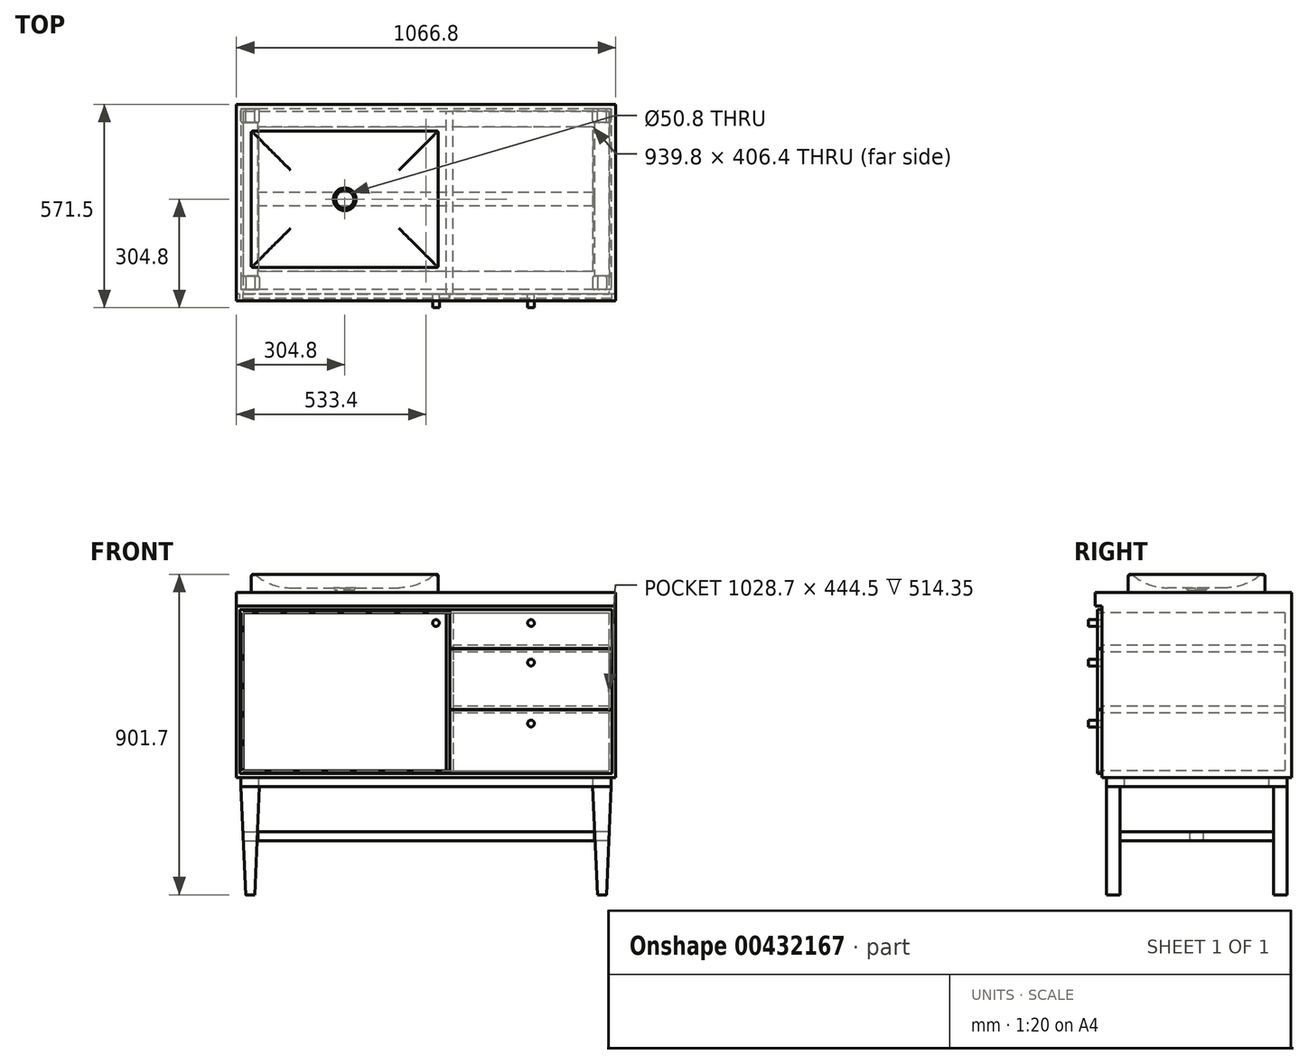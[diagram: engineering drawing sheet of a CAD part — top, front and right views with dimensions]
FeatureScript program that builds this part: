
annotation { "Feature Type Name" : "Feature", "Feature Type Description" : "" }
export const myFeature = defineFeature(function(context is Context, id is Id, definition is map)
    precondition{}
    {
        {
            var Q0;
            Q0=qCreatedBy(makeId("Front.planeOp"),FACE);
            var sketch = newSketch(context, id + "F0", { "sketchPlane" : qUnion([Q0])});
            skLineSegment(sketch, "E0.bottom", {"start": v(533.4, -241.3) * mm, "end": v(-533.4, -241.3) * mm});
            skLineSegment(sketch, "E0.top", {"start": v(533.4, 241.3) * mm, "end": v(-533.4, 241.3) * mm});
            skLineSegment(sketch, "E0.left", {"start": v(533.4, -241.3) * mm, "end": v(533.4, 241.3) * mm});
            skLineSegment(sketch, "E0.right", {"start": v(-533.4, -241.3) * mm, "end": v(-533.4, 241.3) * mm});
            skPoint(sketch, "E0.middle", {"position": v(0, 0) * mm});
            skSolve(sketch);
        }
        {
            var Q0;
            Q0=makeQuery(id+"F0.imprint","IMPRINT",FACE,{"disambiguationData":[TD([[makeQuery(id+"F0.imprint","IMPRINT",EDGE,{"derivedFrom":sQuery(id+"F0.wireOp",EDGE,"E0.bottom")}),-1.0]])]});
            extrude(context, id + "F1", {"entities" : qUnion([Q0]), "oppositeDirection" : true, "depth" : 533.4 * mm});
        }
        {
            var Q0;
            Q0=makeQuery(id+"F1.opExtrude","CAP_FACE",FACE,{"disambiguationData":[OSD([sQuery(id+"F0.wireOp",EDGE,"E0.bottom"),sQuery(id+"F0.wireOp",EDGE,"E0.top"),sQuery(id+"F0.wireOp",EDGE,"E0.left"),sQuery(id+"F0.wireOp",EDGE,"E0.right")])],"isStart":true});
            var sketch = newSketch(context, id + "F2", { "sketchPlane" : qUnion([Q0])});
            skLineSegment(sketch, "E1.bottom", {"start": v(-514.35, 222.25) * mm, "end": v(514.35, 222.25) * mm});
            skLineSegment(sketch, "E1.top", {"start": v(-514.35, -222.25) * mm, "end": v(514.35, -222.25) * mm});
            skLineSegment(sketch, "E1.left", {"start": v(-514.35, 222.25) * mm, "end": v(-514.35, -222.25) * mm});
            skLineSegment(sketch, "E1.right", {"start": v(514.35, 222.25) * mm, "end": v(514.35, -222.25) * mm});
            skPoint(sketch, "E1.middle", {"position": v(0, 0) * mm});
            skSolve(sketch);
        }
        {
            var Q0;
            Q0=makeQuery(id+"F2.imprint","IMPRINT",FACE,{"disambiguationData":[TD([[makeQuery(id+"F2.imprint","IMPRINT",EDGE,{"derivedFrom":sQuery(id+"F2.wireOp",EDGE,"E1.bottom")}),-1.0]])]});
            extrude(context, id + "F3", {"entities" : qUnion([Q0]), "operationType" : NewBodyOperationType.REMOVE, "oppositeDirection" : true, "depth" : 514.35 * mm});
        }
        {
            var Q0;
            Q0=makeQuery(id+"F1.opExtrude","SWEPT_FACE",FACE,{"disambiguationData":[OSD([sQuery(id+"F0.wireOp",EDGE,"E0.bottom")])]});
            var sketch = newSketch(context, id + "F4", { "sketchPlane" : qUnion([Q0])});
            skLineSegment(sketch, "E2.bottom", {"start": v(520.7, -520.7) * mm, "end": v(-520.7, -520.7) * mm});
            skLineSegment(sketch, "E2.top", {"start": v(520.7, -12.7) * mm, "end": v(-520.7, -12.7) * mm});
            skLineSegment(sketch, "E2.left", {"start": v(520.7, -520.7) * mm, "end": v(520.7, -12.7) * mm});
            skLineSegment(sketch, "E2.right", {"start": v(-520.7, -520.7) * mm, "end": v(-520.7, -12.7) * mm});
            skPoint(sketch, "E2.middle", {"position": v(0, -266.7) * mm});
            skPoint(sketch, "E2.middle.positionSnap0", {"position": v(-533.4, -266.7) * mm});
            skPoint(sketch, "E2.centerSnap0", {"position": v(-533.4, -266.7) * mm});
            skLineSegment(sketch, "E3.bottom", {"start": v(469.9, -63.5) * mm, "end": v(-469.9, -63.5) * mm});
            skLineSegment(sketch, "E3.top", {"start": v(469.9, -469.9) * mm, "end": v(-469.9, -469.9) * mm});
            skLineSegment(sketch, "E3.left", {"start": v(469.9, -63.5) * mm, "end": v(469.9, -469.9) * mm});
            skLineSegment(sketch, "E3.right", {"start": v(-469.9, -63.5) * mm, "end": v(-469.9, -469.9) * mm});
            skSolve(sketch);
        }
        {
            var Q0;
            Q0=makeQuery(id+"F4.imprint","IMPRINT",FACE,{"disambiguationData":[TD([[makeQuery(id+"F4.imprint","IMPRINT",EDGE,{"derivedFrom":sQuery(id+"F4.wireOp",EDGE,"E2.bottom")}),-1.0]])]});
            extrude(context, id + "F5", {"entities" : qUnion([Q0]), "depth" : 25.4 * mm});
        }
        {
            var Q0;
            Q0=makeQuery(id+"F5.opExtrude","SWEPT_FACE",FACE,{"disambiguationData":[OSD([sQuery(id+"F4.wireOp",EDGE,"E2.top")])]});
            var sketch = newSketch(context, id + "F6", { "sketchPlane" : qUnion([Q0])});
            skLineSegment(sketch, "E4", {"start": v(-520.7, -266.7) * mm, "end": v(-507.4, -571.5) * mm});
            skLineSegment(sketch, "E5", {"start": v(0, 222.25) * mm, "end": v(0, -222.25) * mm, "construction": true});
            skLineSegment(sketch, "E6.MirrorCS", {"start": v(520.7, -266.7) * mm, "end": v(507.4, -571.5) * mm});
            skLineSegment(sketch, "E7", {"start": v(-507.4, -571.5) * mm, "end": v(-482, -571.5) * mm});
            skLineSegment(sketch, "E8", {"start": v(-482, -571.5) * mm, "end": v(-468.68, -266.7) * mm});
            skLineSegment(sketch, "E9.MirrorCS", {"start": v(482, -571.5) * mm, "end": v(468.68, -266.7) * mm});
            skLineSegment(sketch, "E10.MirrorCS", {"start": v(507.4, -571.5) * mm, "end": v(482, -571.5) * mm});
            skLineSegment(sketch, "E11", {"start": v(-520.7, -266.7) * mm, "end": v(-468.68, -266.7) * mm});
            skLineSegment(sketch, "E12", {"start": v(468.68, -266.7) * mm, "end": v(520.7, -266.7) * mm});
            skSolve(sketch);
        }
        {
            var Q0;
            Q0=makeQuery(id+"F6.imprint","IMPRINT",FACE,{"disambiguationData":[TD([[makeQuery(id+"F6.imprint","IMPRINT",EDGE,{"derivedFrom":sQuery(id+"F6.wireOp",EDGE,"E4")}),1.0]])]});
            var Q1;
            Q1=makeQuery(id+"F6.imprint","IMPRINT",FACE,{"disambiguationData":[TD([[makeQuery(id+"F6.imprint","IMPRINT",EDGE,{"derivedFrom":sQuery(id+"F6.wireOp",EDGE,"E6.MirrorCS")}),-1.0]])]});
            extrude(context, id + "F7", {"entities" : qUnion([Q0, Q1]), "oppositeDirection" : true, "depth" : 38.1 * mm});
        }
        {
            var Q0;
            Q0=makeQuery(id+"F1.opExtrude","CAP_FACE",FACE,{"disambiguationData":[OSD([sQuery(id+"F0.wireOp",EDGE,"E0.bottom"),sQuery(id+"F0.wireOp",EDGE,"E0.top"),sQuery(id+"F0.wireOp",EDGE,"E0.left"),sQuery(id+"F0.wireOp",EDGE,"E0.right")])],"isStart":true});
            cPlane(context, id + "F8", {"entities" : qUnion([Q0]), "cplaneType" : CPlaneType.OFFSET, "offset" : 266.7 * mm, "oppositeDirection" : true, "width" : 152.4 * mm, "height" : 152.4 * mm});
        }
        {
            var Q0;
            Q0=makeQuery(id+"F7.opExtrude","SWEPT_BODY",BODY,{"disambiguationData":[OSD([sQuery(id+"F6.wireOp",EDGE,"E4"),sQuery(id+"F6.wireOp",EDGE,"E7"),sQuery(id+"F6.wireOp",EDGE,"E8"),sQuery(id+"F6.wireOp",EDGE,"E11")])]});
            var Q1;
            Q1=makeQuery(id+"F7.opExtrude","SWEPT_BODY",BODY,{"disambiguationData":[OSD([sQuery(id+"F6.wireOp",EDGE,"E6.MirrorCS"),sQuery(id+"F6.wireOp",EDGE,"E9.MirrorCS"),sQuery(id+"F6.wireOp",EDGE,"E10.MirrorCS"),sQuery(id+"F6.wireOp",EDGE,"E12")])]});
            var Q2;
            Q2=qCreatedBy(id+"F8.planeOp",FACE);
            mirror(context, id + "F9", {"entities" : qUnion([Q0, Q1]), "mirrorPlane" : qUnion([Q2])});
        }
        {
            var Q0;
            Q0=makeQuery(id+"F7.opExtrude","SWEPT_FACE",FACE,{"disambiguationData":[OSD([sQuery(id+"F6.wireOp",EDGE,"E4")])]});
            var sketch = newSketch(context, id + "F10", { "sketchPlane" : qUnion([Q0])});
            skLineSegment(sketch, "E13.bottom", {"start": v(-50.8, -370.73) * mm, "end": v(-482.6, -370.73) * mm});
            skLineSegment(sketch, "E13.top", {"start": v(-50.8, -396.13) * mm, "end": v(-482.6, -396.13) * mm});
            skLineSegment(sketch, "E13.left", {"start": v(-50.8, -370.73) * mm, "end": v(-50.8, -396.13) * mm});
            skLineSegment(sketch, "E13.right", {"start": v(-482.6, -370.73) * mm, "end": v(-482.6, -396.13) * mm});
            skPoint(sketch, "E13.middle", {"position": v(-266.7, -383.43) * mm});
            skSolve(sketch);
        }
        {
            var Q0;
            Q0=makeQuery(id+"F9.opPattern","COPY",FACE,{"derivedFrom":makeQuery(id+"F7.opExtrude","CAP_FACE",FACE,{"disambiguationData":[OSD([sQuery(id+"F6.wireOp",EDGE,"E4"),sQuery(id+"F6.wireOp",EDGE,"E7"),sQuery(id+"F6.wireOp",EDGE,"E8"),sQuery(id+"F6.wireOp",EDGE,"E11")])],"isStart":false}),"instanceName":"1"});
            var sketch = newSketch(context, id + "F11", { "sketchPlane" : qUnion([Q0])});
            skLineSegment(sketch, "E14", {"start": v(-515.16, -393.58) * mm, "end": v(-474.22, -393.58) * mm});
            skSolve(sketch);
        }
        {
            var Q0;
            Q0=makeQuery(id+"F10.imprint","IMPRINT",FACE,{"disambiguationData":[TD([[makeQuery(id+"F10.imprint","IMPRINT",EDGE,{"derivedFrom":sQuery(id+"F10.wireOp",EDGE,"E13.bottom")}),1.0]])]});
            var Q1;
            Q1=sQuery(id+"F11.wireOp",EDGE,"E14");
            sweep(context, id + "F12", {"profiles" : qUnion([Q0]), "path" : qUnion([Q1])});
        }
        {
            var Q0;
            Q0=makeQuery(id+"F12.opSweep","SWEPT_BODY",BODY,{"disambiguationData":[OSD([sQuery(id+"F10.wireOp",EDGE,"E13.bottom"),sQuery(id+"F10.wireOp",EDGE,"E13.top"),sQuery(id+"F10.wireOp",EDGE,"E13.left"),sQuery(id+"F10.wireOp",EDGE,"E13.right"),sQuery(id+"F11.wireOp",EDGE,"E14")])]});
            var Q1;
            Q1=qCreatedBy(makeId("Right.planeOp"),FACE);
            mirror(context, id + "F13", {"entities" : qUnion([Q0]), "mirrorPlane" : qUnion([Q1])});
        }
        {
            var Q0;
            Q0=makeQuery(id+"F12.opSweep","SWEPT_FACE",FACE,{"disambiguationData":[OSD([sQuery(id+"F10.wireOp",EDGE,"E13.bottom"),sQuery(id+"F11.wireOp",EDGE,"E14")])]});
            var sketch = newSketch(context, id + "F14", { "sketchPlane" : qUnion([Q0])});
            skLineSegment(sketch, "E15.bottom", {"start": v(473.12, 285.75) * mm, "end": v(-473.12, 285.75) * mm});
            skLineSegment(sketch, "E15.top", {"start": v(473.12, 247.65) * mm, "end": v(-473.12, 247.65) * mm});
            skLineSegment(sketch, "E15.left", {"start": v(473.12, 285.75) * mm, "end": v(473.12, 247.65) * mm});
            skLineSegment(sketch, "E15.right", {"start": v(-473.12, 285.75) * mm, "end": v(-473.12, 247.65) * mm});
            skPoint(sketch, "E15.middle", {"position": v(0, 266.7) * mm});
            skPoint(sketch, "E15.middle.positionSnap0", {"position": v(-474.22, 266.7) * mm});
            skPoint(sketch, "E15.centerSnap0", {"position": v(-474.22, 266.7) * mm});
            skSolve(sketch);
        }
        {
            var Q0;
            Q0=makeQuery(id+"F14.imprint","IMPRINT",FACE,{"disambiguationData":[TD([[makeQuery(id+"F14.imprint","IMPRINT",EDGE,{"derivedFrom":sQuery(id+"F14.wireOp",EDGE,"E15.bottom")}),1.0]])]});
            var Q1;
            Q1=makeQuery(id+"F12.opSweep","SWEPT_FACE",FACE,{"disambiguationData":[OSD([sQuery(id+"F10.wireOp",EDGE,"E13.top"),sQuery(id+"F11.wireOp",EDGE,"E14")])]});
            extrude(context, id + "F15", {"entities" : qUnion([Q0]), "endBound" : BoundingType.UP_TO_SURFACE, "oppositeDirection" : true, "endBoundEntityFace" : qUnion([Q1]), "depth" : 25.4 * mm});
        }
        {
            var Q0;
            Q0=makeQuery(id+"F1.opExtrude","SWEPT_FACE",FACE,{"disambiguationData":[OSD([sQuery(id+"F0.wireOp",EDGE,"E0.top")])]});
            var sketch = newSketch(context, id + "F16", { "sketchPlane" : qUnion([Q0])});
            skLineSegment(sketch, "E16.bottom", {"start": v(-533.4, 533.4) * mm, "end": v(533.4, 533.4) * mm});
            skLineSegment(sketch, "E16.top", {"start": v(-533.4, 0) * mm, "end": v(533.4, 0) * mm});
            skLineSegment(sketch, "E16.left", {"start": v(-533.4, 533.4) * mm, "end": v(-533.4, 0) * mm});
            skLineSegment(sketch, "E16.right", {"start": v(533.4, 533.4) * mm, "end": v(533.4, 0) * mm});
            skPoint(sketch, "E16.middle", {"position": v(0, 266.7) * mm});
            skPoint(sketch, "E16.middle.positionSnap0", {"position": v(0, 533.4) * mm});
            skPoint(sketch, "E16.middle.positionSnap1", {"position": v(-533.4, 266.7) * mm});
            skPoint(sketch, "E16.centerSnap0", {"position": v(0, 533.4) * mm});
            skPoint(sketch, "E16.centerSnap1", {"position": v(-533.4, 266.7) * mm});
            skSolve(sketch);
        }
        {
            var Q0;
            Q0 = qSketchRegion(id + "F16", true);
            extrude(context, id + "F17", {"entities" : qUnion([Q0]), "depth" : 38.1 * mm});
        }
        {
            var Q0;
            Q0=makeQuery(id+"F17.opExtrude","CAP_FACE",FACE,{"disambiguationData":[OSD([sQuery(id+"F16.wireOp",EDGE,"E16.bottom"),sQuery(id+"F16.wireOp",EDGE,"E16.top"),sQuery(id+"F16.wireOp",EDGE,"E16.left"),sQuery(id+"F16.wireOp",EDGE,"E16.right")])],"isStart":false});
            var sketch = newSketch(context, id + "F18", { "sketchPlane" : qUnion([Q0])});
            skLineSegment(sketch, "E17.bottom", {"start": v(-491.33, 74.61) * mm, "end": v(34.13, 74.61) * mm});
            skLineSegment(sketch, "E17.top", {"start": v(-491.33, 458.79) * mm, "end": v(34.13, 458.79) * mm});
            skLineSegment(sketch, "E17.left", {"start": v(-491.33, 74.61) * mm, "end": v(-491.33, 458.79) * mm});
            skLineSegment(sketch, "E17.right", {"start": v(34.13, 74.61) * mm, "end": v(34.13, 458.79) * mm});
            skPoint(sketch, "E17.middle", {"position": v(-228.6, 266.7) * mm});
            skPoint(sketch, "E17.middle.positionSnap0", {"position": v(533.4, 266.7) * mm});
            skPoint(sketch, "E17.centerSnap0", {"position": v(533.4, 266.7) * mm});
            skSolve(sketch);
        }
        {
            var Q0;
            Q0=makeQuery(id+"F18.imprint","IMPRINT",FACE,{"disambiguationData":[TD([[makeQuery(id+"F18.imprint","IMPRINT",EDGE,{"derivedFrom":sQuery(id+"F18.wireOp",EDGE,"E17.bottom")}),1.0]])]});
            extrude(context, id + "F19", {"entities" : qUnion([Q0]), "depth" : 50.8 * mm});
        }
        {
            var Q0;
            Q0=makeQuery(id+"F19.opExtrude","SWEPT_EDGE",EDGE,{"disambiguationData":[OSD([sQuery(id+"F18.wireOp",EDGE,"E17.bottom"),sQuery(id+"F18.wireOp",EDGE,"E17.left")])]});
            var Q1;
            Q1=makeQuery(id+"F19.opExtrude","SWEPT_EDGE",EDGE,{"disambiguationData":[OSD([sQuery(id+"F18.wireOp",EDGE,"E17.bottom"),sQuery(id+"F18.wireOp",EDGE,"E17.right")])]});
            var Q2;
            Q2=makeQuery(id+"F19.opExtrude","SWEPT_EDGE",EDGE,{"disambiguationData":[OSD([sQuery(id+"F18.wireOp",EDGE,"E17.top"),sQuery(id+"F18.wireOp",EDGE,"E17.right")])]});
            var Q3;
            Q3=makeQuery(id+"F19.opExtrude","SWEPT_EDGE",EDGE,{"disambiguationData":[OSD([sQuery(id+"F18.wireOp",EDGE,"E17.top"),sQuery(id+"F18.wireOp",EDGE,"E17.left")])]});
            fillet(context, id + "F20", {"entities" : qUnion([Q0, Q1, Q2, Q3]), "radius" : (4 + (9 / 16)) * mm, "tangentPropagation" : true, "allowEdgeOverflow" : false});
        }
        {
            var Q0;
            Q0=makeQuery(id+"F19.opExtrude","CAP_FACE",FACE,{"disambiguationData":[OSD([sQuery(id+"F18.wireOp",EDGE,"E17.bottom"),sQuery(id+"F18.wireOp",EDGE,"E17.top"),sQuery(id+"F18.wireOp",EDGE,"E17.left"),sQuery(id+"F18.wireOp",EDGE,"E17.right")])],"isStart":false});
            shell(context, id + "F21", {"entities" : qUnion([Q0]), "thickness" : 12.7 * mm});
        }
        {
            var Q0;
            Q0=makeQuery(id+"F19.opExtrude","CAP_FACE",FACE,{"disambiguationData":[OSD([sQuery(id+"F18.wireOp",EDGE,"E17.bottom"),sQuery(id+"F18.wireOp",EDGE,"E17.top"),sQuery(id+"F18.wireOp",EDGE,"E17.left"),sQuery(id+"F18.wireOp",EDGE,"E17.right")])],"isStart":false});
            fillet(context, id + "F22", {"entities" : qUnion([Q0]), "radius" : 5.08 * mm, "tangentPropagation" : true, "allowEdgeOverflow" : false});
        }
        {
            var Q0;
            Q0=makeQuery(id+"F21.opShell","OFFSET_FACE",FACE,{"disambiguationData":[OSD([sQuery(id+"F18.wireOp",EDGE,"E17.bottom"),sQuery(id+"F18.wireOp",EDGE,"E17.top"),sQuery(id+"F18.wireOp",EDGE,"E17.left"),sQuery(id+"F18.wireOp",EDGE,"E17.right")])]});
            fillet(context, id + "F23", {"entities" : qUnion([Q0]), "radius" : 152.4 * mm, "tangentPropagation" : true, "allowEdgeOverflow" : false});
        }
        {
            var Q0;
            Q0=makeQuery(id+"F21.opShell","OFFSET_FACE",FACE,{"disambiguationData":[OSD([sQuery(id+"F18.wireOp",EDGE,"E17.bottom"),sQuery(id+"F18.wireOp",EDGE,"E17.top"),sQuery(id+"F18.wireOp",EDGE,"E17.left"),sQuery(id+"F18.wireOp",EDGE,"E17.right")])]});
            var sketch = newSketch(context, id + "F24", { "sketchPlane" : qUnion([Q0])});
            skPoint(sketch, "E18", {"position": v(-228.6, 266.7) * mm});
            skPoint(sketch, "E18.positionSnap0", {"position": v(-381, 266.7) * mm});
            skPoint(sketch, "E18.positionSnap1", {"position": v(-228.6, 348.46) * mm});
            skSolve(sketch);
        }
        {
            var Q0;
            Q0=sQuery(id+"F24.wireOp",VERTEX,"E18");
            var Q1;
            Q1=makeQuery(id+"F19.opExtrude","SWEPT_BODY",BODY,{"disambiguationData":[OSD([sQuery(id+"F18.wireOp",EDGE,"E17.bottom"),sQuery(id+"F18.wireOp",EDGE,"E17.top"),sQuery(id+"F18.wireOp",EDGE,"E17.left"),sQuery(id+"F18.wireOp",EDGE,"E17.right")])]});
            hole(context, id + "F25", {"style" : HoleStyle.C_SINK, "endStyle" : HoleEndStyle.BLIND, "holeDiameter" : 50.8 * mm, "cSinkDiameter" : 63.5 * mm, "cSinkAngle" : 82 * degree, "holeDepth" : 25.4 * mm, "isTappedThrough" : true, "tappedDepth" : 12.7 * mm, "tapClearance" : 3, "locations" : qUnion([Q0]), "scope" : qUnion([Q1])});
        }
        {
            var Q0;
            Q0=makeQuery(id+"F12.opSweep","CAP_EDGE",EDGE,{"disambiguationData":[OSD([sQuery(id+"F10.wireOp",EDGE,"E13.top"),sQuery(id+"F11.wireOp",VERTEX,"E14.end")])],"isStart":false});
            var Q1;
            Q1=makeQuery(id+"F12.opSweep","CAP_EDGE",EDGE,{"disambiguationData":[OSD([sQuery(id+"F10.wireOp",EDGE,"E13.bottom"),sQuery(id+"F11.wireOp",VERTEX,"E14.end")])],"isStart":false});
            var Q2;
            Q2=makeQuery(id+"F12.opSweep","CAP_EDGE",EDGE,{"disambiguationData":[OSD([sQuery(id+"F10.wireOp",EDGE,"E13.bottom"),sQuery(id+"F11.wireOp",VERTEX,"E14.start")])],"isStart":true});
            var Q3;
            Q3=makeQuery(id+"F12.opSweep","CAP_EDGE",EDGE,{"disambiguationData":[OSD([sQuery(id+"F10.wireOp",EDGE,"E13.top"),sQuery(id+"F11.wireOp",VERTEX,"E14.start")])],"isStart":true});
            var Q4;
            Q4=makeQuery(id+"F9.opPattern","COPY",EDGE,{"derivedFrom":makeQuery(id+"F7.opExtrude","CAP_EDGE",EDGE,{"disambiguationData":[OSD([sQuery(id+"F6.wireOp",EDGE,"E4")])],"isStart":false}),"instanceName":"1"});
            var Q5;
            Q5=makeQuery(id+"F9.opPattern","COPY",EDGE,{"derivedFrom":makeQuery(id+"F7.opExtrude","CAP_EDGE",EDGE,{"disambiguationData":[OSD([sQuery(id+"F6.wireOp",EDGE,"E8")])],"isStart":false}),"instanceName":"1"});
            var Q6;
            Q6=makeQuery(id+"F9.opPattern","COPY",EDGE,{"derivedFrom":makeQuery(id+"F7.opExtrude","CAP_EDGE",EDGE,{"disambiguationData":[OSD([sQuery(id+"F6.wireOp",EDGE,"E4")])],"isStart":true}),"instanceName":"1"});
            var Q7;
            Q7=makeQuery(id+"F15.opExtrude","CAP_EDGE",EDGE,{"disambiguationData":[OSD([sQuery(id+"F14.wireOp",EDGE,"E15.top")])],"isStart":true});
            var Q8;
            Q8=makeQuery(id+"F7.opExtrude","CAP_EDGE",EDGE,{"disambiguationData":[OSD([sQuery(id+"F6.wireOp",EDGE,"E4")])],"isStart":true});
            var Q9;
            Q9=makeQuery(id+"F7.opExtrude","CAP_EDGE",EDGE,{"disambiguationData":[OSD([sQuery(id+"F6.wireOp",EDGE,"E4")])],"isStart":false});
            var Q10;
            Q10=makeQuery(id+"F7.opExtrude","CAP_EDGE",EDGE,{"disambiguationData":[OSD([sQuery(id+"F6.wireOp",EDGE,"E8")])],"isStart":true});
            var Q11;
            Q11=makeQuery(id+"F7.opExtrude","CAP_EDGE",EDGE,{"disambiguationData":[OSD([sQuery(id+"F6.wireOp",EDGE,"E8")])],"isStart":false});
            var Q12;
            Q12=makeQuery(id+"F9.opPattern","COPY",EDGE,{"derivedFrom":makeQuery(id+"F7.opExtrude","CAP_EDGE",EDGE,{"disambiguationData":[OSD([sQuery(id+"F6.wireOp",EDGE,"E8")])],"isStart":true}),"instanceName":"1"});
            var Q13;
            Q13=makeQuery(id+"F15.opExtrude","CAP_EDGE",EDGE,{"disambiguationData":[OSD([sQuery(id+"F14.wireOp",EDGE,"E15.top")])],"isStart":false});
            var Q14;
            Q14=makeQuery(id+"F15.opExtrude","CAP_EDGE",EDGE,{"disambiguationData":[OSD([sQuery(id+"F14.wireOp",EDGE,"E15.bottom")])],"isStart":true});
            var Q15;
            Q15=makeQuery(id+"F15.opExtrude","CAP_EDGE",EDGE,{"disambiguationData":[OSD([sQuery(id+"F14.wireOp",EDGE,"E15.bottom")])],"isStart":false});
            var Q16;
            Q16=makeQuery(id+"F13.opPattern","COPY",EDGE,{"derivedFrom":makeQuery(id+"F12.opSweep","CAP_EDGE",EDGE,{"disambiguationData":[OSD([sQuery(id+"F10.wireOp",EDGE,"E13.top"),sQuery(id+"F11.wireOp",VERTEX,"E14.end")])],"isStart":false}),"instanceName":"1"});
            var Q17;
            Q17=makeQuery(id+"F13.opPattern","COPY",EDGE,{"derivedFrom":makeQuery(id+"F12.opSweep","CAP_EDGE",EDGE,{"disambiguationData":[OSD([sQuery(id+"F10.wireOp",EDGE,"E13.bottom"),sQuery(id+"F11.wireOp",VERTEX,"E14.end")])],"isStart":false}),"instanceName":"1"});
            var Q18;
            Q18=makeQuery(id+"F9.opPattern","COPY",EDGE,{"derivedFrom":makeQuery(id+"F7.opExtrude","CAP_EDGE",EDGE,{"disambiguationData":[OSD([sQuery(id+"F6.wireOp",EDGE,"E9.MirrorCS")])],"isStart":false}),"instanceName":"1"});
            var Q19;
            Q19=makeQuery(id+"F9.opPattern","COPY",EDGE,{"derivedFrom":makeQuery(id+"F7.opExtrude","CAP_EDGE",EDGE,{"disambiguationData":[OSD([sQuery(id+"F6.wireOp",EDGE,"E9.MirrorCS")])],"isStart":true}),"instanceName":"1"});
            var Q20;
            Q20=makeQuery(id+"F9.opPattern","COPY",EDGE,{"derivedFrom":makeQuery(id+"F7.opExtrude","CAP_EDGE",EDGE,{"disambiguationData":[OSD([sQuery(id+"F6.wireOp",EDGE,"E6.MirrorCS")])],"isStart":true}),"instanceName":"1"});
            var Q21;
            Q21=makeQuery(id+"F9.opPattern","COPY",EDGE,{"derivedFrom":makeQuery(id+"F7.opExtrude","CAP_EDGE",EDGE,{"disambiguationData":[OSD([sQuery(id+"F6.wireOp",EDGE,"E6.MirrorCS")])],"isStart":false}),"instanceName":"1"});
            var Q22;
            Q22=makeQuery(id+"F13.opPattern","COPY",EDGE,{"derivedFrom":makeQuery(id+"F12.opSweep","CAP_EDGE",EDGE,{"disambiguationData":[OSD([sQuery(id+"F10.wireOp",EDGE,"E13.bottom"),sQuery(id+"F11.wireOp",VERTEX,"E14.start")])],"isStart":true}),"instanceName":"1"});
            var Q23;
            Q23=makeQuery(id+"F13.opPattern","COPY",EDGE,{"derivedFrom":makeQuery(id+"F12.opSweep","CAP_EDGE",EDGE,{"disambiguationData":[OSD([sQuery(id+"F10.wireOp",EDGE,"E13.top"),sQuery(id+"F11.wireOp",VERTEX,"E14.start")])],"isStart":true}),"instanceName":"1"});
            var Q24;
            Q24=makeQuery(id+"F7.opExtrude","CAP_EDGE",EDGE,{"disambiguationData":[OSD([sQuery(id+"F6.wireOp",EDGE,"E6.MirrorCS")])],"isStart":true});
            var Q25;
            Q25=makeQuery(id+"F7.opExtrude","CAP_EDGE",EDGE,{"disambiguationData":[OSD([sQuery(id+"F6.wireOp",EDGE,"E6.MirrorCS")])],"isStart":false});
            var Q26;
            Q26=makeQuery(id+"F7.opExtrude","CAP_EDGE",EDGE,{"disambiguationData":[OSD([sQuery(id+"F6.wireOp",EDGE,"E9.MirrorCS")])],"isStart":false});
            var Q27;
            Q27=makeQuery(id+"F7.opExtrude","CAP_EDGE",EDGE,{"disambiguationData":[OSD([sQuery(id+"F6.wireOp",EDGE,"E9.MirrorCS")])],"isStart":true});
            fillet(context, id + "F26", {"entities" : qUnion([Q0, Q1, Q2, Q3, Q4, Q5, Q6, Q7, Q8, Q9, Q10, Q11, Q12, Q13, Q14, Q15, Q16, Q17, Q18, Q19, Q20, Q21, Q22, Q23, Q24, Q25, Q26, Q27]), "radius" : 5.08 * mm, "tangentPropagation" : true, "allowEdgeOverflow" : false});
        }
        {
            var Q0;
            Q0=makeQuery(id+"F3.boolean.opBoolean","COPY",FACE,{"derivedFrom":makeQuery(id+"F3.opExtrude","CAP_FACE",FACE,{"disambiguationData":[OSD([sQuery(id+"F2.wireOp",EDGE,"E1.bottom"),sQuery(id+"F2.wireOp",EDGE,"E1.top"),sQuery(id+"F2.wireOp",EDGE,"E1.left"),sQuery(id+"F2.wireOp",EDGE,"E1.right")])],"isStart":false})});
            var sketch = newSketch(context, id + "F27", { "sketchPlane" : qUnion([Q0])});
            skLineSegment(sketch, "E19.bottom", {"start": v(57.15, 222.25) * mm, "end": v(76.2, 222.25) * mm});
            skLineSegment(sketch, "E19.top", {"start": v(57.15, -222.25) * mm, "end": v(76.2, -222.25) * mm});
            skLineSegment(sketch, "E19.left", {"start": v(57.15, 222.25) * mm, "end": v(57.15, -222.25) * mm});
            skLineSegment(sketch, "E19.right", {"start": v(76.2, 222.25) * mm, "end": v(76.2, -222.25) * mm});
            skPoint(sketch, "E19.middle", {"position": v(66.67, 0) * mm});
            skSolve(sketch);
        }
        {
            var Q0;
            Q0=makeQuery(id+"F27.imprint","IMPRINT",FACE,{"disambiguationData":[TD([[makeQuery(id+"F27.imprint","IMPRINT",EDGE,{"derivedFrom":sQuery(id+"F27.wireOp",EDGE,"E19.bottom")}),-1.0]])]});
            var Q1;
            Q1=makeQuery(id+"F1.opExtrude","CAP_FACE",FACE,{"disambiguationData":[OSD([sQuery(id+"F0.wireOp",EDGE,"E0.bottom"),sQuery(id+"F0.wireOp",EDGE,"E0.top"),sQuery(id+"F0.wireOp",EDGE,"E0.left"),sQuery(id+"F0.wireOp",EDGE,"E0.right")])],"isStart":true});
            extrude(context, id + "F28", {"entities" : qUnion([Q0]), "endBound" : BoundingType.UP_TO_SURFACE, "endBoundEntityFace" : qUnion([Q1]), "depth" : 25.4 * mm});
        }
        {
            var Q0;
            Q0=makeQuery(id+"F1.opExtrude","CAP_FACE",FACE,{"disambiguationData":[OSD([sQuery(id+"F0.wireOp",EDGE,"E0.bottom"),sQuery(id+"F0.wireOp",EDGE,"E0.top"),sQuery(id+"F0.wireOp",EDGE,"E0.left"),sQuery(id+"F0.wireOp",EDGE,"E0.right")])],"isStart":true});
            var sketch = newSketch(context, id + "F29", { "sketchPlane" : qUnion([Q0])});
            skLineSegment(sketch, "E20.bottom", {"start": v(65.88, 230.98) * mm, "end": v(-523.08, 230.98) * mm});
            skLineSegment(sketch, "E20.top", {"start": v(65.88, -230.98) * mm, "end": v(-523.08, -230.98) * mm});
            skLineSegment(sketch, "E20.left", {"start": v(65.88, 230.98) * mm, "end": v(65.88, -230.98) * mm});
            skLineSegment(sketch, "E20.right", {"start": v(-523.08, 230.98) * mm, "end": v(-523.08, -230.98) * mm});
            skPoint(sketch, "E20.middle", {"position": v(-228.6, 0) * mm});
            skSolve(sketch);
        }
        {
            var Q0;
            Q0=makeQuery(id+"F29.imprint","IMPRINT",FACE,{"disambiguationData":[TD([[makeQuery(id+"F29.imprint","IMPRINT",EDGE,{"derivedFrom":sQuery(id+"F29.wireOp",EDGE,"E20.bottom")}),1.0]])]});
            var Q1;
            {var subQ5=makeQuery(id+"F3.boolean.opBoolean","COPY",EDGE,{"derivedFrom":makeQuery(id+"F3.opExtrude","CAP_EDGE",EDGE,{"disambiguationData":[OSD([sQuery(id+"F2.wireOp",EDGE,"E1.left")])],"isStart":true})});Q1=makeQuery(id+"F29.imprint","IMPRINT",FACE,{"disambiguationData":[TD([[makeQuery(id+"F29.imprint","IMPRINT",EDGE,{"derivedFrom":subQ5}),1.0]])]});}
            extrude(context, id + "F30", {"entities" : qUnion([Q0, Q1]), "depth" : 12.7 * mm});
        }
        {
            var Q0;
            Q0=makeQuery(id+"F1.opExtrude","CAP_FACE",FACE,{"disambiguationData":[OSD([sQuery(id+"F0.wireOp",EDGE,"E0.bottom"),sQuery(id+"F0.wireOp",EDGE,"E0.top"),sQuery(id+"F0.wireOp",EDGE,"E0.left"),sQuery(id+"F0.wireOp",EDGE,"E0.right")])],"isStart":true});
            var sketch = newSketch(context, id + "F31", { "sketchPlane" : qUnion([Q0])});
            skLineSegment(sketch, "E21.bottom", {"start": v(514.35, 111.12) * mm, "end": v(76.2, 111.12) * mm});
            skLineSegment(sketch, "E21.top", {"start": v(514.35, 130.17) * mm, "end": v(76.2, 130.17) * mm});
            skLineSegment(sketch, "E21.left", {"start": v(514.35, 111.12) * mm, "end": v(514.35, 130.17) * mm});
            skLineSegment(sketch, "E21.right", {"start": v(76.2, 111.12) * mm, "end": v(76.2, 130.17) * mm});
            skPoint(sketch, "E21.middle", {"position": v(295.27, 120.65) * mm});
            skLineSegment(sketch, "E22.bottom", {"start": v(514.35, -41.27) * mm, "end": v(76.2, -41.27) * mm});
            skLineSegment(sketch, "E22.top", {"start": v(514.35, -60.32) * mm, "end": v(76.2, -60.32) * mm});
            skLineSegment(sketch, "E22.left", {"start": v(514.35, -41.27) * mm, "end": v(514.35, -60.32) * mm});
            skLineSegment(sketch, "E22.right", {"start": v(76.2, -41.27) * mm, "end": v(76.2, -60.32) * mm});
            skPoint(sketch, "E22.middle", {"position": v(295.27, -50.8) * mm});
            skLineSegment(sketch, "E23", {"start": v(295.27, 120.65) * mm, "end": v(295.27, -222.25) * mm, "construction": true});
            skSolve(sketch);
        }
        {
            var Q0;
            Q0=makeQuery(id+"F31.imprint","IMPRINT",FACE,{"disambiguationData":[TD([[makeQuery(id+"F31.imprint","IMPRINT",EDGE,{"derivedFrom":sQuery(id+"F31.wireOp",EDGE,"E21.bottom")}),-1.0]])]});
            var Q1;
            Q1=makeQuery(id+"F31.imprint","IMPRINT",FACE,{"disambiguationData":[TD([[makeQuery(id+"F31.imprint","IMPRINT",EDGE,{"derivedFrom":sQuery(id+"F31.wireOp",EDGE,"E22.bottom")}),1.0]])]});
            extrude(context, id + "F32", {"entities" : qUnion([Q0, Q1]), "oppositeDirection" : true, "depth" : 514.35 * mm});
        }
        {
            var Q0;
            Q0=makeQuery(id+"F1.opExtrude","CAP_FACE",FACE,{"disambiguationData":[OSD([sQuery(id+"F0.wireOp",EDGE,"E0.bottom"),sQuery(id+"F0.wireOp",EDGE,"E0.top"),sQuery(id+"F0.wireOp",EDGE,"E0.left"),sQuery(id+"F0.wireOp",EDGE,"E0.right")])],"isStart":true});
            var sketch = newSketch(context, id + "F33", { "sketchPlane" : qUnion([Q0])});
            skLineSegment(sketch, "E24.bottom", {"start": v(523.08, -230.98) * mm, "end": v(67.47, -230.98) * mm});
            skLineSegment(sketch, "E24.top", {"start": v(523.08, -51.6) * mm, "end": v(67.47, -51.6) * mm});
            skLineSegment(sketch, "E24.left", {"start": v(523.08, -230.98) * mm, "end": v(523.08, -51.6) * mm});
            skLineSegment(sketch, "E24.right", {"start": v(67.47, -230.98) * mm, "end": v(67.47, -51.6) * mm});
            skPoint(sketch, "E24.middle", {"position": v(295.27, -141.29) * mm});
            skLineSegment(sketch, "E25.bottom", {"start": v(523.08, -50) * mm, "end": v(67.47, -50) * mm});
            skLineSegment(sketch, "E25.top", {"start": v(523.08, 119.86) * mm, "end": v(67.47, 119.86) * mm});
            skLineSegment(sketch, "E25.left", {"start": v(523.08, -50) * mm, "end": v(523.08, 119.86) * mm});
            skLineSegment(sketch, "E25.right", {"start": v(67.47, -50) * mm, "end": v(67.47, 119.86) * mm});
            skPoint(sketch, "E25.middle", {"position": v(295.27, 34.92) * mm});
            skLineSegment(sketch, "E26.bottom", {"start": v(523.08, 121.44) * mm, "end": v(67.47, 121.44) * mm});
            skLineSegment(sketch, "E26.top", {"start": v(523.08, 230.98) * mm, "end": v(67.47, 230.98) * mm});
            skLineSegment(sketch, "E26.left", {"start": v(523.08, 121.44) * mm, "end": v(523.08, 230.98) * mm});
            skLineSegment(sketch, "E26.right", {"start": v(67.47, 121.44) * mm, "end": v(67.47, 230.98) * mm});
            skPoint(sketch, "E26.middle", {"position": v(295.27, 176.21) * mm});
            skSolve(sketch);
        }
        {
            var Q0;
            {var subQ0=sQuery(id+"F33.wireOp",EDGE,"E25.right");Q0=makeQuery(id+"F33.imprint","IMPRINT",FACE,{"disambiguationData":[TD([[makeQuery(id+"F33.imprint","IMPRINT",EDGE,{"derivedFrom":subQ0}),-1.0]])]});}
            var Q1;
            {var subQ0=sQuery(id+"F33.wireOp",EDGE,"E25.left");Q1=makeQuery(id+"F33.imprint","IMPRINT",FACE,{"disambiguationData":[TD([[makeQuery(id+"F33.imprint","IMPRINT",EDGE,{"derivedFrom":subQ0}),1.0]])]});}
            var Q2;
            {var subQ0=sQuery(id+"F33.wireOp",EDGE,"E26.right");var subQ1=sQuery(id+"F33.wireOp",EDGE,"E26.bottom");var subQ2=makeQuery(id+"F33.imprint","INTERSECT",VERTEX,{"derivedFrom":[subQ1,subQ0]});Q2=makeQuery(id+"F33.imprint","IMPRINT",FACE,{"disambiguationData":[TD([[makeQuery(id+"F33.imprint","IMPRINT",EDGE,{"disambiguationData":[TD([[subQ2,1.0]])],"derivedFrom":subQ1}),-1.0]])]});}
            var Q3;
            {var subQ1=sQuery(id+"F33.wireOp",EDGE,"E26.top");Q3=makeQuery(id+"F33.imprint","IMPRINT",FACE,{"disambiguationData":[TD([[makeQuery(id+"F33.imprint","IMPRINT",EDGE,{"derivedFrom":subQ1}),1.0]])]});}
            var Q4;
            {var subQ0=sQuery(id+"F33.wireOp",EDGE,"E24.right");var subQ1=sQuery(id+"F33.wireOp",EDGE,"E24.top");var subQ2=makeQuery(id+"F33.imprint","INTERSECT",VERTEX,{"derivedFrom":[subQ1,subQ0]});Q4=makeQuery(id+"F33.imprint","IMPRINT",FACE,{"disambiguationData":[TD([[makeQuery(id+"F33.imprint","IMPRINT",EDGE,{"disambiguationData":[TD([[subQ2,1.0]])],"derivedFrom":subQ1}),1.0]])]});}
            var Q5;
            {var subQ1=sQuery(id+"F33.wireOp",EDGE,"E24.bottom");Q5=makeQuery(id+"F33.imprint","IMPRINT",FACE,{"disambiguationData":[TD([[makeQuery(id+"F33.imprint","IMPRINT",EDGE,{"derivedFrom":subQ1}),-1.0]])]});}
            extrude(context, id + "F34", {"entities" : qUnion([Q0, Q1, Q2, Q3, Q4, Q5]), "depth" : 12.7 * mm});
        }
        {
            var Q0;
            Q0=makeQuery(id+"F34.opExtrude","CAP_FACE",FACE,{"disambiguationData":[OSD([sQuery(id+"F33.wireOp",EDGE,"E24.bottom"),sQuery(id+"F33.wireOp",EDGE,"E24.top"),sQuery(id+"F33.wireOp",EDGE,"E24.left"),sQuery(id+"F33.wireOp",EDGE,"E24.right")])],"isStart":true});
            var sketch = newSketch(context, id + "F35", { "sketchPlane" : qUnion([Q0])});
            skCircle(sketch, "E27", {"center": v(-295.27, -89.7) * mm, "radius": 9.53 * mm});
            skPoint(sketch, "E27.centerSnap0", {"position": v(-295.27, -51.6) * mm});
            skCircle(sketch, "E28", {"center": v(-295.27, 81.76) * mm, "radius": 9.53 * mm});
            skCircle(sketch, "E29", {"center": v(-295.27, 192.88) * mm, "radius": 9.53 * mm});
            skCircle(sketch, "E30", {"center": v(-27.78, 192.88) * mm, "radius": 9.53 * mm});
            skSolve(sketch);
        }
        {
            var Q0;
            Q0=makeQuery(id+"F35.imprint","IMPRINT",FACE,{"disambiguationData":[TD([[makeQuery(id+"F35.imprint","IMPRINT",EDGE,{"derivedFrom":sQuery(id+"F35.wireOp",EDGE,"E30")}),1.0]])]});
            var Q1;
            Q1=makeQuery(id+"F35.imprint","IMPRINT",FACE,{"disambiguationData":[TD([[makeQuery(id+"F35.imprint","IMPRINT",EDGE,{"derivedFrom":sQuery(id+"F35.wireOp",EDGE,"E29")}),1.0]])]});
            var Q2;
            Q2=makeQuery(id+"F35.imprint","IMPRINT",FACE,{"disambiguationData":[TD([[makeQuery(id+"F35.imprint","IMPRINT",EDGE,{"derivedFrom":sQuery(id+"F35.wireOp",EDGE,"E28")}),1.0]])]});
            var Q3;
            Q3=makeQuery(id+"F35.imprint","IMPRINT",FACE,{"disambiguationData":[TD([[makeQuery(id+"F35.imprint","IMPRINT",EDGE,{"derivedFrom":sQuery(id+"F35.wireOp",EDGE,"E27")}),1.0]])]});
            extrude(context, id + "F36", {"entities" : qUnion([Q0, Q1, Q2, Q3]), "oppositeDirection" : true, "depth" : 38.1 * mm});
        }
        {
            var Q0;
            Q0=makeQuery(id+"F17.opExtrude","SWEPT_FACE",FACE,{"disambiguationData":[OSD([sQuery(id+"F16.wireOp",EDGE,"E16.top")])]});
            extrude(context, id + "F37", {"entities" : qUnion([Q0]), "operationType" : NewBodyOperationType.ADD, "depth" : 19.05 * mm});
        }
    });
